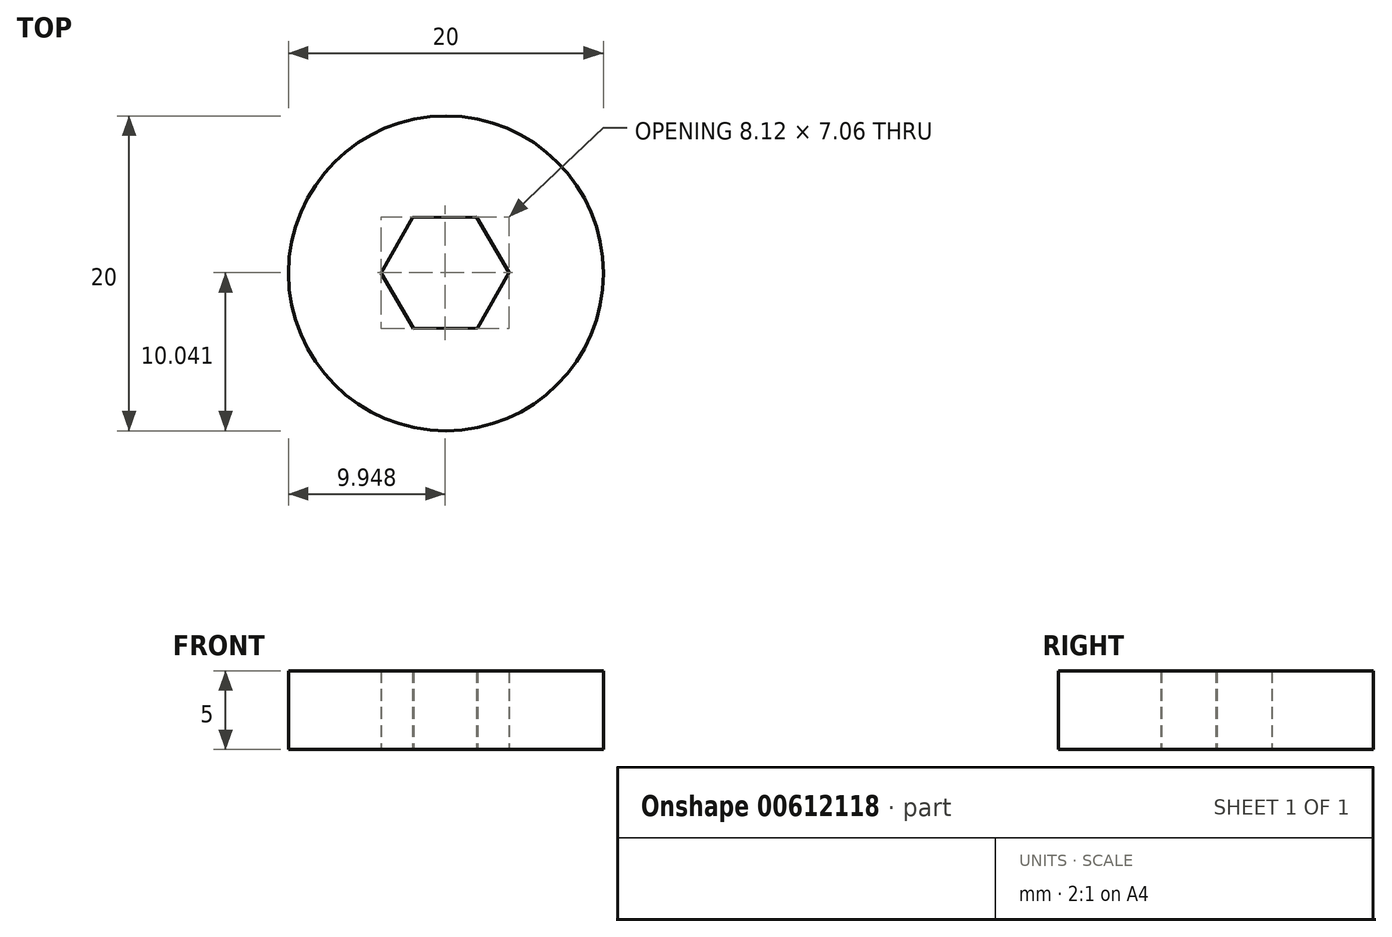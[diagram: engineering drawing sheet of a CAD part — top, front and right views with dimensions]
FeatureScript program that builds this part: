
annotation { "Feature Type Name" : "Feature", "Feature Type Description" : "" }
export const myFeature = defineFeature(function(context is Context, id is Id, definition is map)
    precondition{}
    {
        {
            var Q0;
            Q0=qCreatedBy(makeId("Top.planeOp"),FACE);
            var sketch = newSketch(context, id + "F0", { "sketchPlane" : qUnion([Q0])});
            skCircle(sketch, "E0.cCircle", {"center": v(-0.05, 0.04) * mm, "radius": 4.06 * mm, "construction": true});
            skLineSegment(sketch, "E0.0", {"start": v(1.96, 3.57) * mm, "end": v(4, 0.07) * mm});
            skLineSegment(sketch, "E0.1", {"start": v(4, 0.07) * mm, "end": v(2, -3.46) * mm});
            skLineSegment(sketch, "E0.2", {"start": v(2, -3.46) * mm, "end": v(-2.06, -3.49) * mm});
            skLineSegment(sketch, "E0.3", {"start": v(-2.06, -3.49) * mm, "end": v(-4.11, 0.02) * mm});
            skLineSegment(sketch, "E0.4", {"start": v(-4.11, 0.02) * mm, "end": v(-2.1, 3.55) * mm});
            skLineSegment(sketch, "E0.5", {"start": v(-2.1, 3.55) * mm, "end": v(1.96, 3.57) * mm});
            skCircle(sketch, "E1", {"center": v(0, 0) * mm, "radius": 10 * mm});
            skSolve(sketch);
        }
        {
            var Q0;
            Q0=makeQuery(id+"F0.imprint","IMPRINT",FACE,{"disambiguationData":[TD([[makeQuery(id+"F0.imprint","IMPRINT",EDGE,{"derivedFrom":sQuery(id+"F0.wireOp",EDGE,"E0.0")}),1.0]])]});
            extrude(context, id + "F1", {"entities" : qUnion([Q0]), "depth" : 5 * mm, "offsetDistance" : 25 * mm});
        }
    });
